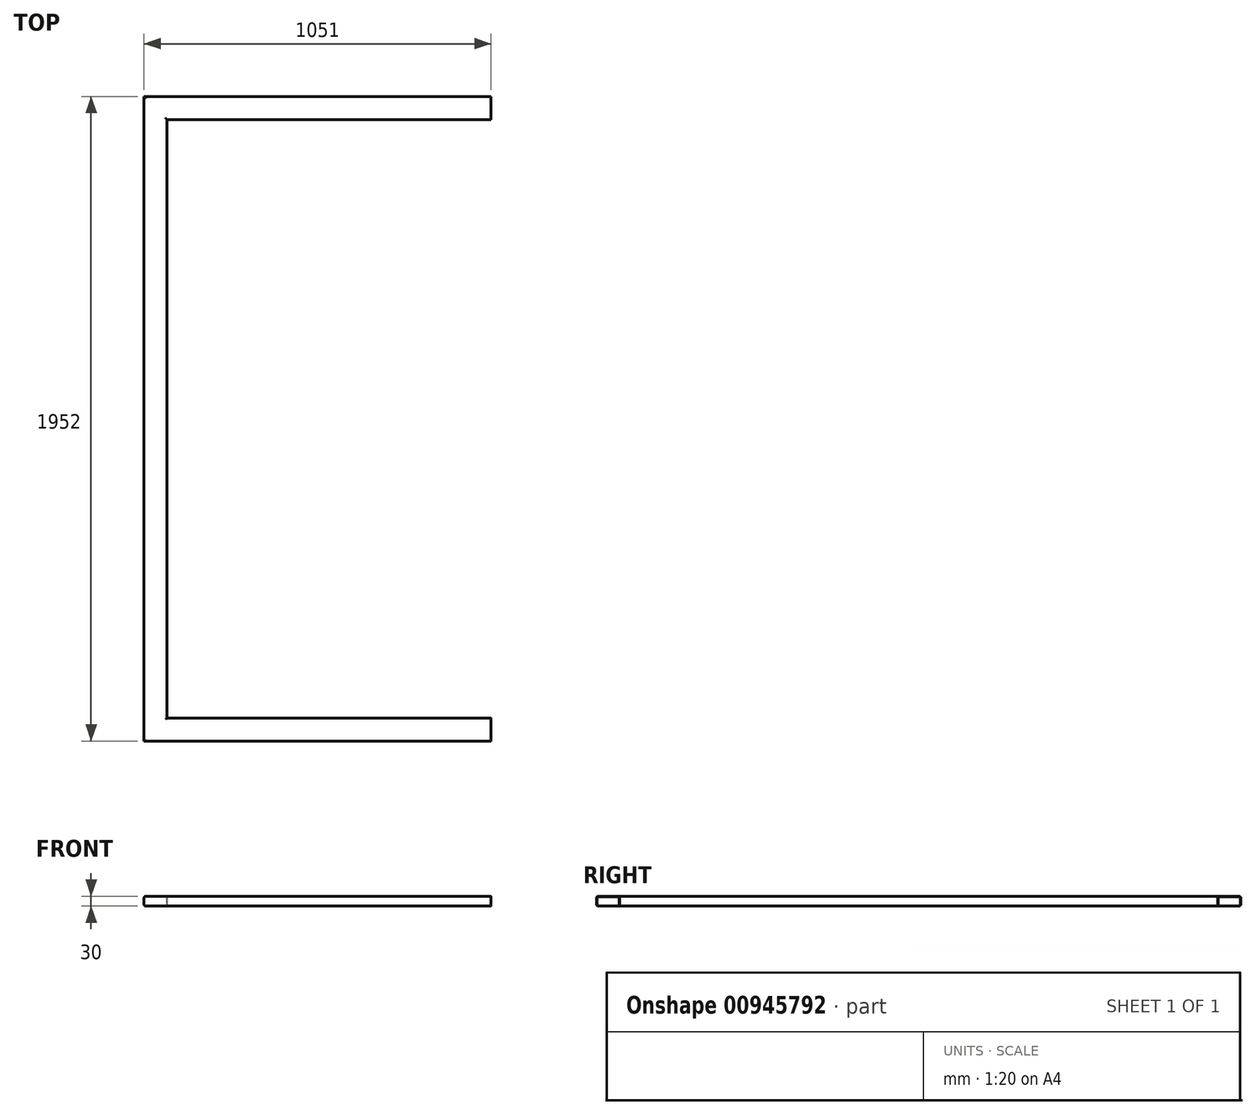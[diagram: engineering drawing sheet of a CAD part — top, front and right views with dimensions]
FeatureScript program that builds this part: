
annotation { "Feature Type Name" : "Feature", "Feature Type Description" : "" }
export const myFeature = defineFeature(function(context is Context, id is Id, definition is map)
    precondition{}
    {
        {
            var Q0;
            Q0=qCreatedBy(makeId("Right.planeOp"),FACE);
            var sketch = newSketch(context, id + "F0", { "sketchPlane" : qUnion([Q0])});
            skLineSegment(sketch, "E0.bottom", {"start": v(30, 15) * mm, "end": v(-30, 15) * mm});
            skLineSegment(sketch, "E0.top", {"start": v(30, -15) * mm, "end": v(-30, -15) * mm});
            skLineSegment(sketch, "E0.left", {"start": v(35, 10) * mm, "end": v(35, -10) * mm});
            skLineSegment(sketch, "E0.right", {"start": v(-35, 10) * mm, "end": v(-35, -10) * mm});
            skPoint(sketch, "E0.middle", {"position": v(0, 0) * mm});
            skPoint(sketch, "E1.visualSharp", {"position": v(-35, -15) * mm});
            skArc(sketch, "E1.filletArc", {"start": v(-35, -10) * mm, "mid": v(-33.54, -13.54) * mm, "end": v(-30, -15) * mm});
            skPoint(sketch, "E2.visualSharp", {"position": v(-35, 15) * mm});
            skArc(sketch, "E2.filletArc", {"start": v(-30, 15) * mm, "mid": v(-33.54, 13.54) * mm, "end": v(-35, 10) * mm});
            skPoint(sketch, "E3.visualSharp", {"position": v(35, 15) * mm});
            skArc(sketch, "E3.filletArc", {"start": v(35, 10) * mm, "mid": v(33.54, 13.54) * mm, "end": v(30, 15) * mm});
            skPoint(sketch, "E4.visualSharp", {"position": v(35, -15) * mm});
            skArc(sketch, "E4.filletArc", {"start": v(30, -15) * mm, "mid": v(33.54, -13.54) * mm, "end": v(35, -10) * mm});
            skArc(sketch, "E5.0", {"start": v(34, 10) * mm, "mid": v(32.83, 12.83) * mm, "end": v(30, 14) * mm});
            skLineSegment(sketch, "E5.1", {"start": v(34, 10) * mm, "end": v(34, -10) * mm});
            skLineSegment(sketch, "E5.2", {"start": v(30, 14) * mm, "end": v(-30, 14) * mm});
            skArc(sketch, "E5.3", {"start": v(30, -14) * mm, "mid": v(32.83, -12.83) * mm, "end": v(34, -10) * mm});
            skArc(sketch, "E5.4", {"start": v(-30, 14) * mm, "mid": v(-32.83, 12.83) * mm, "end": v(-34, 10) * mm});
            skLineSegment(sketch, "E5.5", {"start": v(-34, 10) * mm, "end": v(-34, -10) * mm});
            skArc(sketch, "E5.6", {"start": v(-34, -10) * mm, "mid": v(-32.83, -12.83) * mm, "end": v(-30, -14) * mm});
            skLineSegment(sketch, "E5.7", {"start": v(30, -14) * mm, "end": v(-30, -14) * mm});
            skSolve(sketch);
        }
        {
            var Q0;
            Q0=qCreatedBy(makeId("Top.planeOp"),FACE);
            var sketch = newSketch(context, id + "F1", { "sketchPlane" : qUnion([Q0])});
            skLineSegment(sketch, "E6", {"start": v(0, 0) * mm, "end": v(-1016, 0) * mm});
            skLineSegment(sketch, "E7", {"start": v(-1016, 0) * mm, "end": v(-1016, 1882) * mm});
            skLineSegment(sketch, "E8", {"start": v(-1016, 1882) * mm, "end": v(0, 1882) * mm});
            skSolve(sketch);
        }
        {
            var Q0;
            Q0=makeQuery(id+"F0.imprint","IMPRINT",FACE,{"disambiguationData":[TD([[makeQuery(id+"F0.imprint","IMPRINT",EDGE,{"derivedFrom":sQuery(id+"F0.wireOp",EDGE,"E0.bottom")}),1.0]])]});
            var Q1;
            Q1=sQuery(id+"F1.wireOp",EDGE,"E6");
            var Q2;
            Q2=sQuery(id+"F1.wireOp",EDGE,"E7");
            var Q3;
            Q3=sQuery(id+"F1.wireOp",EDGE,"E8");
            sweep(context, id + "F2", {"profiles" : qUnion([Q0]), "path" : qUnion([Q1, Q2, Q3])});
        }
    });
